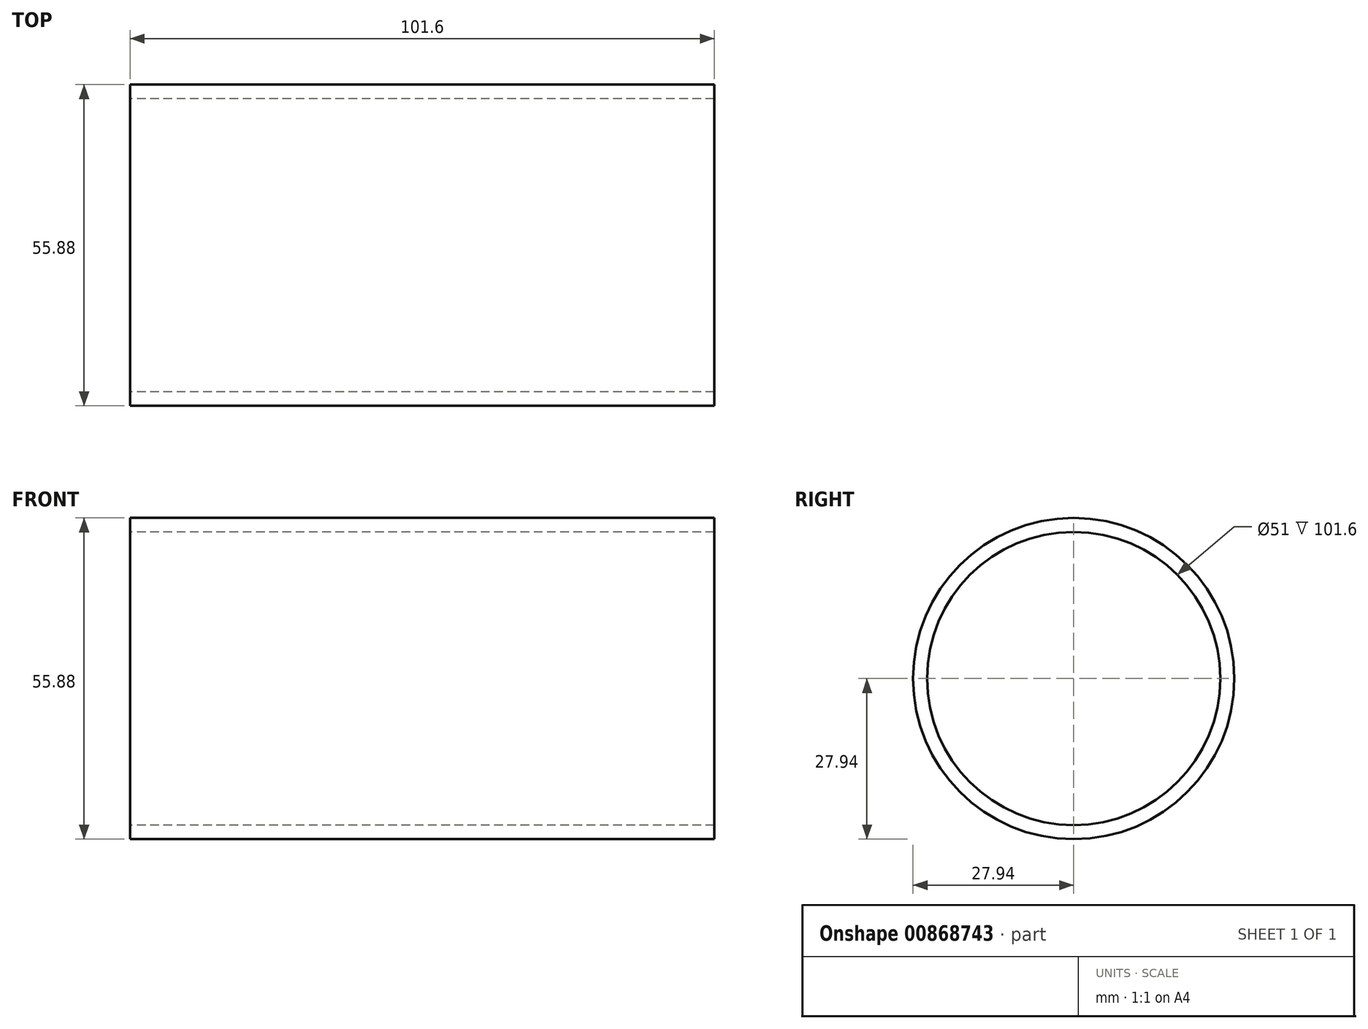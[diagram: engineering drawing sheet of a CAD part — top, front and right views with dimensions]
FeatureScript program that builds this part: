
annotation { "Feature Type Name" : "Feature", "Feature Type Description" : "" }
export const myFeature = defineFeature(function(context is Context, id is Id, definition is map)
    precondition{}
    {
        {
            var Q0;
            Q0=qCreatedBy(makeId("Right.planeOp"),FACE);
            var sketch = newSketch(context, id + "F0", { "sketchPlane" : qUnion([Q0])});
            skCircle(sketch, "E0", {"center": v(0, 0) * mm, "radius": 27.94 * mm});
            skCircle(sketch, "E1", {"center": v(0, 0) * mm, "radius": 25.5 * mm});
            skSolve(sketch);
        }
        {
            var Q0;
            Q0=makeQuery(id+"F0.imprint","IMPRINT",FACE,{"disambiguationData":[TD([[makeQuery(id+"F0.imprint","IMPRINT",EDGE,{"derivedFrom":sQuery(id+"F0.wireOp",EDGE,"E0")}),1.0]])]});
            extrude(context, id + "F1", {"entities" : qUnion([Q0]), "depth" : 101.6 * mm, "offsetDistance" : 25.4 * mm});
        }
    });
